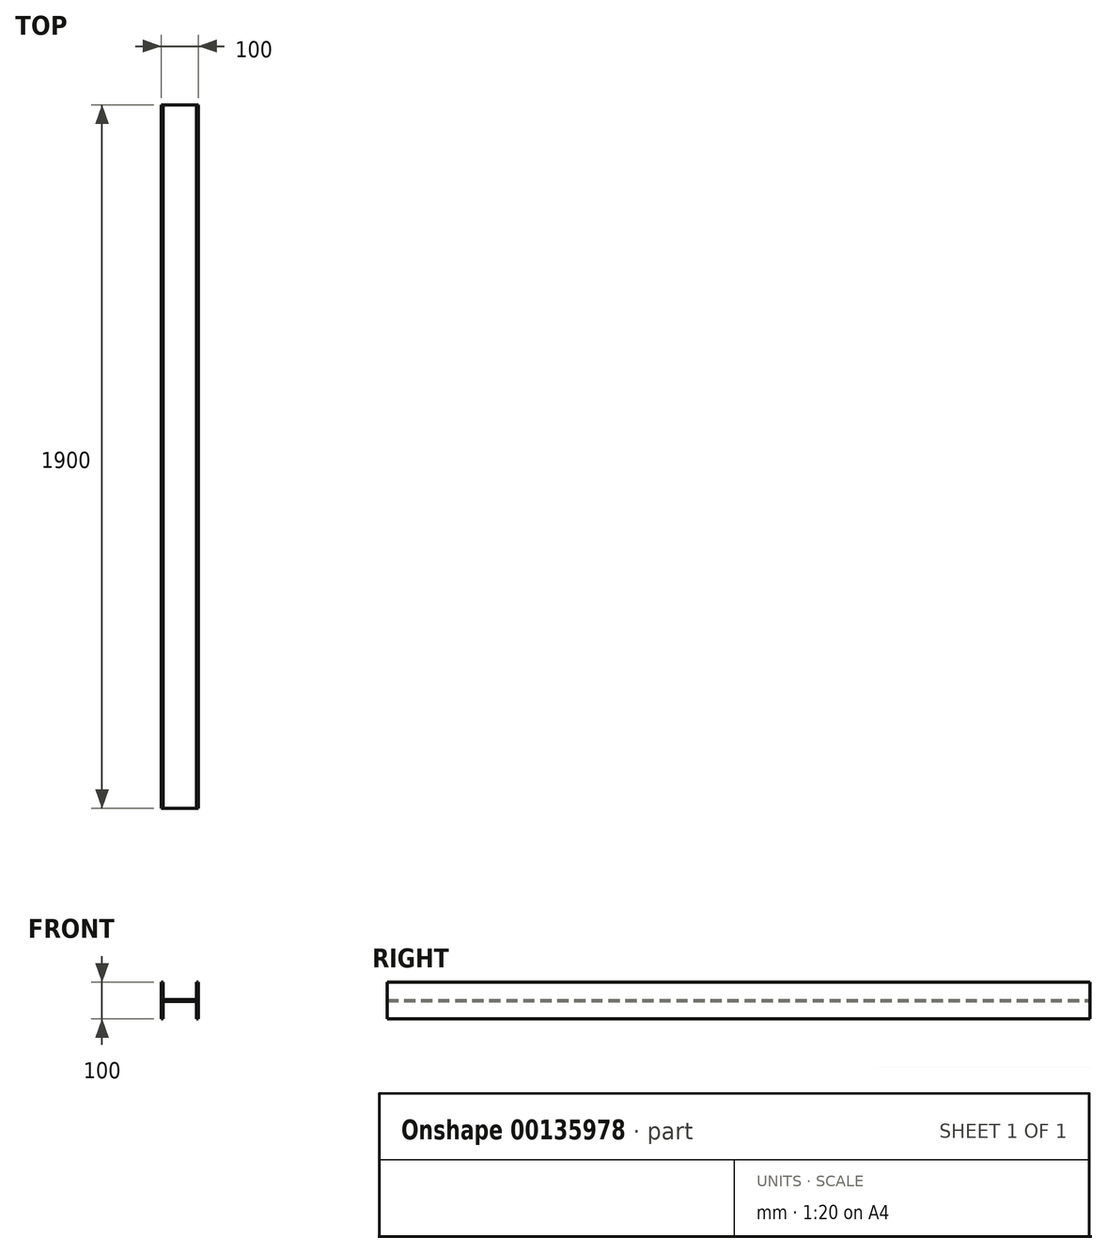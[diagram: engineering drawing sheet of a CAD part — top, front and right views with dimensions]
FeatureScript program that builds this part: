
annotation { "Feature Type Name" : "Feature", "Feature Type Description" : "" }
export const myFeature = defineFeature(function(context is Context, id is Id, definition is map)
    precondition{}
    {
        {
            var Q0;
            Q0=qCreatedBy(makeId("Front.planeOp"),FACE);
            var sketch = newSketch(context, id + "F0", { "sketchPlane" : qUnion([Q0])});
            skLineSegment(sketch, "E0", {"start": v(-50, -50) * mm, "end": v(-50, 50) * mm});
            skLineSegment(sketch, "E1", {"start": v(-50, 50) * mm, "end": v(-45, 50) * mm});
            skLineSegment(sketch, "E2", {"start": v(-45, 50) * mm, "end": v(-45, 2.5) * mm});
            skLineSegment(sketch, "E3", {"start": v(-45, 2.5) * mm, "end": v(45, 2.5) * mm});
            skLineSegment(sketch, "E4", {"start": v(45, 2.5) * mm, "end": v(45, 50) * mm});
            skPoint(sketch, "E4.endSnap0", {"position": v(-47.5, 50) * mm});
            skLineSegment(sketch, "E5", {"start": v(45, 50) * mm, "end": v(50, 50) * mm});
            skLineSegment(sketch, "E6", {"start": v(50, 50) * mm, "end": v(50, -50) * mm});
            skLineSegment(sketch, "E7", {"start": v(50, -50) * mm, "end": v(45, -50) * mm});
            skLineSegment(sketch, "E8", {"start": v(45, -50) * mm, "end": v(45, -2.5) * mm});
            skLineSegment(sketch, "E9", {"start": v(45, -2.5) * mm, "end": v(-45, -2.5) * mm});
            skLineSegment(sketch, "E10", {"start": v(-45, -2.5) * mm, "end": v(-45, -50) * mm});
            skLineSegment(sketch, "E11", {"start": v(-45, -50) * mm, "end": v(-50, -50) * mm});
            skSolve(sketch);
        }
        {
            var Q0;
            Q0=makeQuery(id+"F0.imprint","IMPRINT",FACE,{"disambiguationData":[TD([[makeQuery(id+"F0.imprint","IMPRINT",EDGE,{"derivedFrom":sQuery(id+"F0.wireOp",EDGE,"E0")}),-1.0]])]});
            extrude(context, id + "F1", {"entities" : qUnion([Q0]), "endBound" : BoundingType.SYMMETRIC, "depth" : 1900 * mm});
        }
    });
